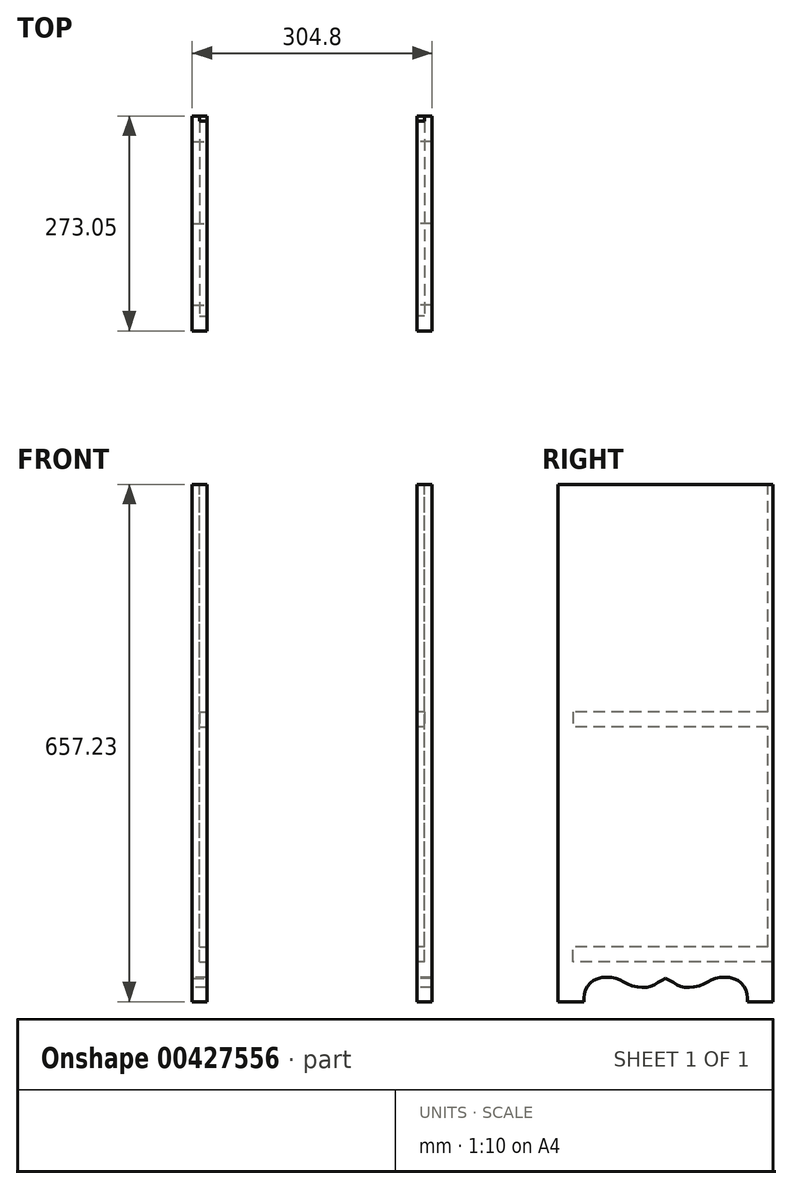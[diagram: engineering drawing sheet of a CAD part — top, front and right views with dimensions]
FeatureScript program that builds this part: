
annotation { "Feature Type Name" : "Feature", "Feature Type Description" : "" }
export const myFeature = defineFeature(function(context is Context, id is Id, definition is map)
    precondition{}
    {
        {
            var Q0;
            Q0=qCreatedBy(makeId("Front.planeOp"),FACE);
            var sketch = newSketch(context, id + "F0", { "sketchPlane" : qUnion([Q0])});
            skLineSegment(sketch, "E0.bottom", {"start": v(0, 0) * mm, "end": v(19.05, 0) * mm});
            skLineSegment(sketch, "E0.top", {"start": v(0, 657.23) * mm, "end": v(19.05, 657.23) * mm});
            skLineSegment(sketch, "E0.left", {"start": v(0, 0) * mm, "end": v(0, 657.23) * mm});
            skLineSegment(sketch, "E0.right", {"start": v(19.05, 0) * mm, "end": v(19.05, 657.23) * mm});
            skSolve(sketch);
        }
        {
            var Q0;
            Q0 = qSketchRegion(id + "F0", true);
            extrude(context, id + "F1", {"entities" : qUnion([Q0]), "depth" : 273.05 * mm});
        }
        {
            var Q0;
            Q0=makeQuery(id+"F1.opExtrude","SWEPT_FACE",FACE,{"disambiguationData":[OSD([sQuery(id+"F0.wireOp",EDGE,"E0.right")])]});
            var sketch = newSketch(context, id + "F2", { "sketchPlane" : qUnion([Q0])});
            skLineSegment(sketch, "E1.bottom", {"start": v(0, 368.3) * mm, "end": v(-254, 368.3) * mm});
            skLineSegment(sketch, "E1.top", {"start": v(0, 349.25) * mm, "end": v(-254, 349.25) * mm});
            skLineSegment(sketch, "E1.left", {"start": v(0, 368.3) * mm, "end": v(0, 349.25) * mm});
            skLineSegment(sketch, "E1.right", {"start": v(-254, 368.3) * mm, "end": v(-254, 349.25) * mm});
            skLineSegment(sketch, "E2.bottom", {"start": v(0, 50.8) * mm, "end": v(-254, 50.8) * mm});
            skLineSegment(sketch, "E2.top", {"start": v(0, 69.85) * mm, "end": v(-254, 69.85) * mm});
            skLineSegment(sketch, "E2.left", {"start": v(0, 50.8) * mm, "end": v(0, 69.85) * mm});
            skLineSegment(sketch, "E2.right", {"start": v(-254, 50.8) * mm, "end": v(-254, 69.85) * mm});
            skLineSegment(sketch, "E3.bottom", {"start": v(0, 69.85) * mm, "end": v(-6.35, 69.85) * mm});
            skLineSegment(sketch, "E3.top", {"start": v(0, 657.23) * mm, "end": v(-6.35, 657.23) * mm});
            skLineSegment(sketch, "E3.left", {"start": v(0, 69.85) * mm, "end": v(0, 657.23) * mm});
            skLineSegment(sketch, "E3.right", {"start": v(-6.35, 69.85) * mm, "end": v(-6.35, 657.23) * mm});
            skSolve(sketch);
        }
        {
            var Q0;
            Q0 = qSketchRegion(id + "F2", true);
            extrude(context, id + "F3", {"entities" : qUnion([Q0]), "operationType" : NewBodyOperationType.REMOVE, "oppositeDirection" : true, "depth" : 9.52 * mm});
        }
        {
            var Q0;
            Q0=makeQuery(id+"F1.opExtrude","SWEPT_FACE",FACE,{"disambiguationData":[OSD([sQuery(id+"F0.wireOp",EDGE,"E0.right")])]});
            var sketch = newSketch(context, id + "F4", { "sketchPlane" : qUnion([Q0])});
            skLineSegment(sketch, "E4", {"start": v(-136.53, 0) * mm, "end": v(-136.53, 59.3) * mm});
            skFitSpline(sketch, "E5", {"points": [v(-240.25, 0) * mm, v(-238.89, 12.66) * mm, v(-230.89, 25.04) * mm, v(-216.52, 30.77) * mm, v(-197.78, 29.2) * mm, v(-184.55, 22.09) * mm, v(-163.23, 17.94) * mm, v(-150.61, 21.88) * mm, v(-136.53, 29.65) * mm], "startDerivative": vector(0.98, 111.8) * mm, "endDerivative": vector(107.23, 49.7) * mm});
            skFitSpline(sketch, "E6.MirrorCS", {"points": [v(-32.8, 0) * mm, v(-34.16, 12.66) * mm, v(-42.16, 25.04) * mm, v(-56.53, 30.77) * mm, v(-75.27, 29.2) * mm, v(-88.5, 22.09) * mm, v(-109.82, 17.94) * mm, v(-122.44, 21.88) * mm, v(-136.53, 29.65) * mm], "startDerivative": vector(-0.98, 111.8) * mm, "endDerivative": vector(-107.23, 49.7) * mm});
            skLineSegment(sketch, "E7", {"start": v(-240.25, 0) * mm, "end": v(-32.8, 0) * mm});
            skSolve(sketch);
        }
        {
            var Q0;
            Q0 = qSketchRegion(id + "F4", true);
            extrude(context, id + "F5", {"entities" : qUnion([Q0]), "operationType" : NewBodyOperationType.REMOVE, "oppositeDirection" : true, "depth" : 25.4 * mm});
        }
        {
            var Q0;
            Q0=qCreatedBy(makeId("Right.planeOp"),FACE);
            cPlane(context, id + "F6", {"entities" : qUnion([Q0]), "cplaneType" : CPlaneType.OFFSET, "offset" : 152.4 * mm, "width" : 152.4 * mm, "height" : 152.4 * mm});
        }
        {
            var Q0;
            Q0=makeQuery(id+"F1.opExtrude","SWEPT_BODY",BODY,{"disambiguationData":[OSD([sQuery(id+"F0.wireOp",EDGE,"E0.bottom"),sQuery(id+"F0.wireOp",EDGE,"E0.top"),sQuery(id+"F0.wireOp",EDGE,"E0.left"),sQuery(id+"F0.wireOp",EDGE,"E0.right")])]});
            var Q1;
            Q1=qCreatedBy(id+"F6.planeOp",FACE);
            mirror(context, id + "F7", {"entities" : qUnion([Q0]), "mirrorPlane" : qUnion([Q1])});
        }
    });
